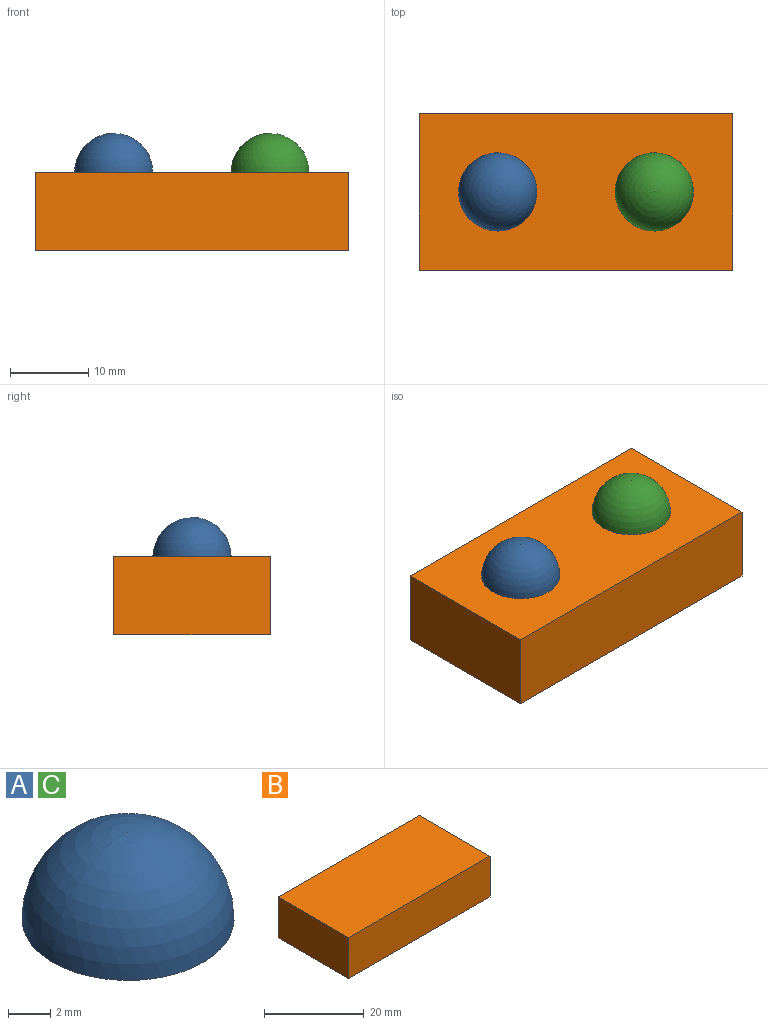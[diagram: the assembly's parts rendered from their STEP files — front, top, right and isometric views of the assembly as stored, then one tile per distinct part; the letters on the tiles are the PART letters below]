
ASSEMBLY  parts=3 mates=2
PART A: 3 faces, bbox 10x10x5 mm
  f0: sphere r=2.5mm, area 39.3mm2, adj f2
  f1: sphere r=5mm, area 157.1mm2, adj f2
  f2: plane 10x10mm, normal (0,0,-1), area 58.9mm2, adj f0,f1
PART B: 6 faces, bbox 40x20x10 mm
  f0: plane 40x10mm, normal (0,-1,0), area 400mm2, adj f1,f3,f4,f5
  f1: plane 20x10mm, normal (1,0,0), area 200mm2, adj f0,f2,f4,f5
  f2: plane 40x10mm, normal (0,1,0), area 400mm2, adj f1,f3,f4,f5
  f3: plane 20x10mm, normal (-1,0,0), area 200mm2, adj f0,f2,f4,f5
  f4: plane 40x20mm, normal (0,0,1), area 800mm2, adj f0,f1,f2,f3
  f5: plane 40x20mm, normal (0,0,-1), area 800mm2, adj f0,f1,f2,f3
PART C: same geometry as A
PLACE A t=(-10,0,0)mm
PLACE B t=(0,0,-10)mm
PLACE C t=(10,0,0)mm
MATE fastened C.f2 <-> B.f4  axis (0,0,-1) through (10,0,0)mm
MATE fastened A.f2 <-> C.f2  axis (0,0,1) through (-10,0,0)mm
